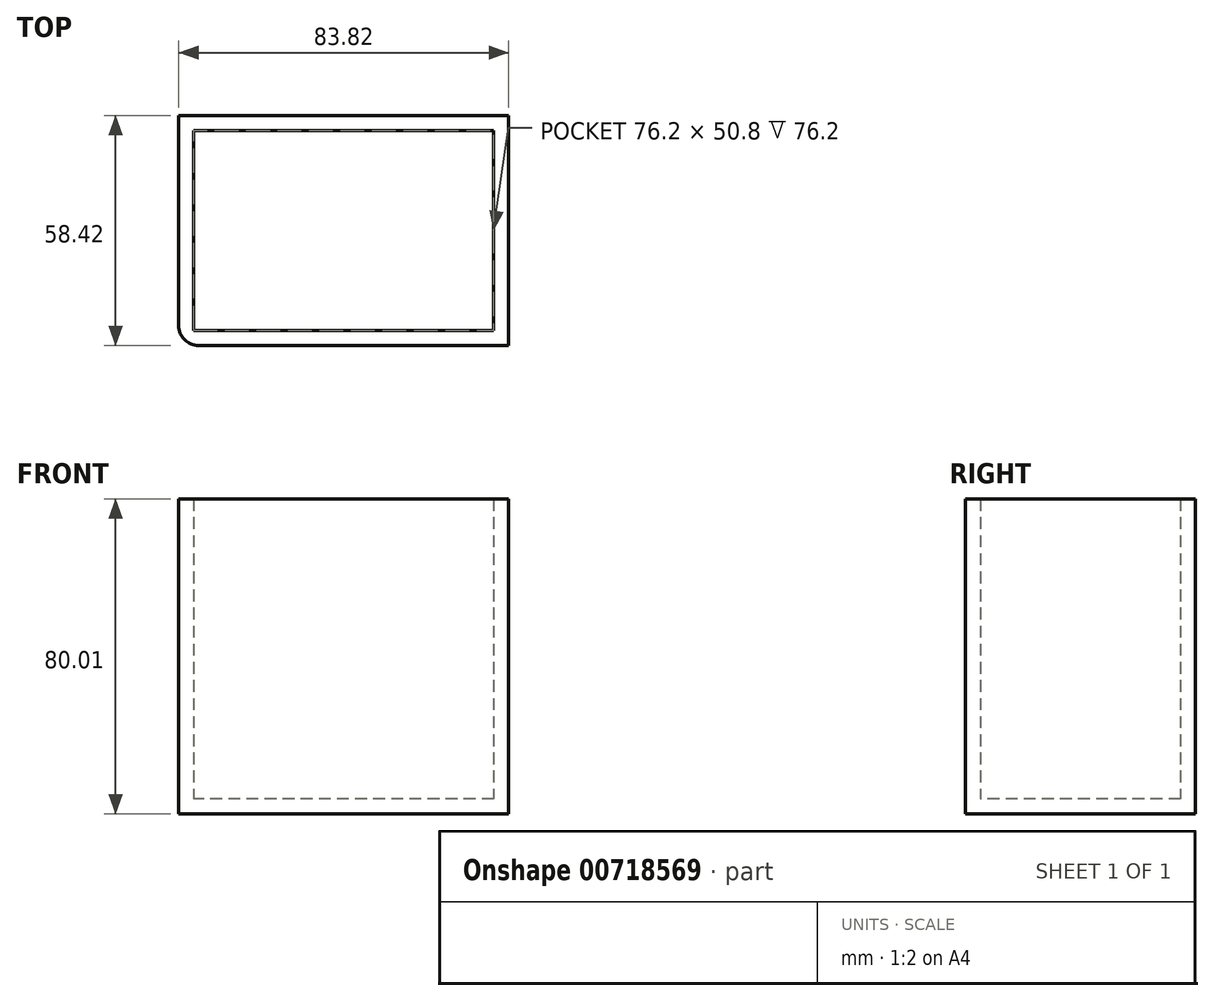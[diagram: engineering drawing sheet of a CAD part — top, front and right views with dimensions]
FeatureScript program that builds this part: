
annotation { "Feature Type Name" : "Feature", "Feature Type Description" : "" }
export const myFeature = defineFeature(function(context is Context, id is Id, definition is map)
    precondition{}
    {
        {
            var Q0;
            Q0=qCreatedBy(makeId("Top.planeOp"),FACE);
            var sketch = newSketch(context, id + "F0", { "sketchPlane" : qUnion([Q0])});
            skLineSegment(sketch, "E0", {"start": v(-80, 50.8) * mm, "end": v(-80, 54.6) * mm});
            skLineSegment(sketch, "E1", {"start": v(-80, 54.6) * mm, "end": v(-76.2, 54.6) * mm});
            skLineSegment(sketch, "E2", {"start": v(3.81, 0) * mm, "end": v(3.81, -3.8) * mm});
            skLineSegment(sketch, "E3", {"start": v(3.81, -3.8) * mm, "end": v(0, -3.8) * mm});
            skLineSegment(sketch, "E4.bottom", {"start": v(-80, 54.6) * mm, "end": v(3.81, 54.6) * mm});
            skLineSegment(sketch, "E4.top", {"start": v(-80, -3.8) * mm, "end": v(3.81, -3.8) * mm});
            skLineSegment(sketch, "E4.left", {"start": v(-80, 54.6) * mm, "end": v(-80, -3.81) * mm});
            skLineSegment(sketch, "E4.right", {"start": v(3.81, 54.6) * mm, "end": v(3.81, -3.81) * mm});
            skPoint(sketch, "E5.end.orphan", {"position": v(0, 0) * mm});
            skPoint(sketch, "E5.start.orphan", {"position": v(0, 50.8) * mm});
            skSolve(sketch);
        }
        {
            var Q0;
            Q0 = qSketchRegion(id + "F0", true);
            extrude(context, id + "F1", {"entities" : qUnion([Q0]), "depth" : 3.8 * mm, "offsetDistance" : 25.4 * mm});
        }
        {
            var Q0;
            Q0=makeQuery(id+"F1.opExtrude","CAP_FACE",FACE,{"disambiguationData":[OSD([sQuery(id+"F0.wireOp",EDGE,"E4.bottom"),sQuery(id+"F0.wireOp",EDGE,"E4.top"),sQuery(id+"F0.wireOp",EDGE,"E4.left"),sQuery(id+"F0.wireOp",EDGE,"E4.right")])],"isStart":false});
            var sketch = newSketch(context, id + "F2", { "sketchPlane" : qUnion([Q0])});
            skLineSegment(sketch, "E6", {"start": v(0, 0) * mm, "end": v(-76.2, 0) * mm});
            skLineSegment(sketch, "E7", {"start": v(-76.2, 0) * mm, "end": v(-76.2, 50.8) * mm});
            skLineSegment(sketch, "E8", {"start": v(-76.2, 50.8) * mm, "end": v(0, 50.8) * mm});
            skLineSegment(sketch, "E9", {"start": v(0, 50.8) * mm, "end": v(0, 0) * mm});
            skPoint(sketch, "E10.end.orphan", {"position": v(3.81, 50.8) * mm});
            skPoint(sketch, "E11.start.orphan", {"position": v(0, 54.6) * mm});
            skLineSegment(sketch, "E12", {"start": v(-76.2, 54.6) * mm, "end": v(-80, 54.6) * mm});
            skLineSegment(sketch, "E13", {"start": v(-80, 54.6) * mm, "end": v(-80, 50.8) * mm});
            skLineSegment(sketch, "E14", {"start": v(0, -3.8) * mm, "end": v(3.81, -3.81) * mm});
            skLineSegment(sketch, "E15", {"start": v(3.81, -3.81) * mm, "end": v(3.81, 0) * mm});
            skLineSegment(sketch, "E16.bottom", {"start": v(-80, 54.6) * mm, "end": v(3.81, 54.6) * mm});
            skLineSegment(sketch, "E16.top", {"start": v(-80, -3.81) * mm, "end": v(3.81, -3.81) * mm});
            skLineSegment(sketch, "E16.left", {"start": v(-80, 54.6) * mm, "end": v(-80, -3.81) * mm});
            skLineSegment(sketch, "E16.right", {"start": v(3.81, 54.6) * mm, "end": v(3.81, 0) * mm});
            skSolve(sketch);
        }
        {
            var Q0;
            Q0 = qSketchRegion(id + "F2", true);
            extrude(context, id + "F3", {"entities" : qUnion([Q0]), "operationType" : NewBodyOperationType.ADD, "depth" : 76.2 * mm, "offsetDistance" : 25.4 * mm});
        }
        {
            var Q0;
            Q0=makeQuery(id+"F3.boolean.opBoolean","MERGE",EDGE,{"derivedFrom":[makeQuery(id+"F1.opExtrude","SWEPT_EDGE",EDGE,{"disambiguationData":[OSD([sQuery(id+"F0.wireOp",EDGE,"E4.top"),sQuery(id+"F0.wireOp",EDGE,"E4.right")])]}),makeQuery(id+"F3.opExtrude","SWEPT_EDGE",EDGE,{"disambiguationData":[OSD([sQuery(id+"F2.wireOp",EDGE,"E15"),sQuery(id+"F2.wireOp",EDGE,"E16.top")])]})]});
            fillet(context, id + "F4", {"entities" : qUnion([Q0]), "radius" : 5.08 * mm, "tangentPropagation" : true, "allowEdgeOverflow" : false});
        }
    });
